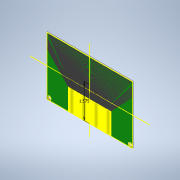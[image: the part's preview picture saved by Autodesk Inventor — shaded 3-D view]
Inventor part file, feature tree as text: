
AUTODESK INVENTOR PART (.ipt)
format: ipt  version: 2021 (Build 250183000, 183)  size: 6,338,560 bytes
history: native  units: in
note: dims shown in document units (in); Inventor stores cm internally (conversion verified against a paired STEP export)
features: sketch x12, extrude x9, projected_geometry x8, pattern_linear x7, mirror x5, hole x1
ambient origin geometry x8: Origin, YZ Plane, XZ Plane, XY Plane, X Axis, Y Axis, Z Axis, Center Point
bodies: Solid1 (feature_tree)
feature tree (42):
  extrude  "Extrusion1"  Depth=2.7in
  hole  "Hole1"  [1 undecoded]
  mirror  "Mirror3"
  sketch  "Sketch9"  dims[d42=0.1in d43=0.11in]
  extrude  "Extrusion5"  Depth=0.11in
  pattern_linear  "Rectangular Pattern6"  Count1=101 Spacing1=0.039in
  extrude  "Extrusion6"  Depth=0.0014in TaperAngle=0.0deg
  pattern_linear  "Rectangular Pattern7"  Count1=101 Spacing1=0.039in
  extrude  "Extrusion7"  TaperAngle=0.0deg  [1 undecoded]
  mirror  "Mirror4"
  extrude  "Extrusion9"  Depth=0.0014in
  pattern_linear  "Rectangular Pattern9"  Spacing1=0.25in  [1 undecoded]
  sketch  "Sketch16"  dims[d54=1.75in]
  pattern_linear  "Rectangular Pattern10"  Spacing1=0.008in  [1 undecoded]
  extrude  "Extrusion10"  Depth=1.0in
  pattern_linear  "Rectangular Pattern11"  Spacing1=0.0014in  [1 undecoded]
  mirror  "Mirror5"
  extrude  "Extrusion11"  Depth=0.016in
  mirror  "Mirror6"
  extrude  "Extrusion12"  Depth=0.0014in
  pattern_linear  "Rectangular Pattern12"  Spacing1=0.0198in  [1 undecoded]
  extrude  "Extrusion13"  Depth=0.0014in
  pattern_linear  "Rectangular Pattern13"  Spacing1=0.175in  [1 undecoded]
  mirror  "Mirror7"
  sketch  "Sketch1"  dims[d0=4.0in d1=2.7in]
  sketch  "Sketch7"  dims[d2=0.04in d3=0.0in d41=0.1719in]
  projected_geometry  "Projected Loop6"
  projected_geometry  "Projected Loop8"
  sketch  "Sketch11"  dims[d44=0.17in d45=0.75in d46=0.313in d47=0.164in d48=0.5635in d49=0.12in]
  projected_geometry  "Projected Loop9"
  sketch  "Sketch12"  dims[d50=0.8108in]
  sketch  "Sketch13"  dims[d52=1.5748in]
  sketch  "Sketch15"  dims[d53=0.02in]
  projected_geometry  "Projected Loop11"
  projected_geometry  "Projected Loop12"
  sketch  "Sketch17"  dims[d55=0.0in d56=0.0in d57=39.7638in d59=0.039in]
  projected_geometry  "Projected Loop13"
  sketch  "Sketch18"  dims[d60=0.032in d61=0.0014in d62=0.0in d63=39.7638in d65=0.039in]
  projected_geometry  "Projected Loop14"
  sketch  "Sketch19"  dims[d66=0.0197in d69=0.0in d70=0.0in]
  projected_geometry  "Projected Loop15"
  sketch  "Sketch20"  dims[d71=2.65in d82=2.0in d83=0.25in d84=0.008in d86=1.0in d87=0.0014in d88=0.0in d89=49.2126in d91=0.016in d92=39.7638in d94=0.039in d95=0.0198in d96=0.05in d97=0.175in d98=0.0in d99=0.0in d100=5.1181in d102=0.039in d103=0.008in d104=0.008in d105=0.008in d106=0.008in d107=0.008in d108=0.008in d109=0.008in d110=0.008in d111=0.008in d112=0.008in d113=0.008in d114=0.008in d115=0.008in d116=0.008in d117=0.008in d118=0.008in d119=0.008in d120=0.008in d121=0.008in d122=0.008in d123=0.008in d124=0.008in d125=0.008in d126=0.008in d127=0.008in d128=0.008in d129=0.008in d130=0.008in d131=0.008in d132=0.008in d133=0.008in d134=0.008in d135=0.008in d136=0.008in d137=0.008in d138=0.008in d139=0.008in d140=0.008in d141=0.008in d142=0.008in d143=0.008in d144=0.008in d145=0.008in d146=0.008in d147=0.008in d148=0.008in d149=0.008in d150=0.008in d151=0.008in d152=0.008in d153=0.008in d154=0.008in d155=0.008in d156=0.008in d157=0.008in d158=0.008in d159=0.008in d160=0.008in d161=0.008in d162=0.008in d163=0.008in d164=0.008in d165=0.008in d166=0.0014in d167=0.0in d168=0.008in d169=0.03in d170=0.0014in d171=0.0in d172=5.1181in d174=0.039in d175=0.032in d176=0.0014in d177=0.0in d178=39.7638in d180=0.039in]
note: 7 required parameter values undecoded (feature->parameter linkage not recoverable at this tier; creation-order binding heuristic only, values carry confidence <= 0.55)
